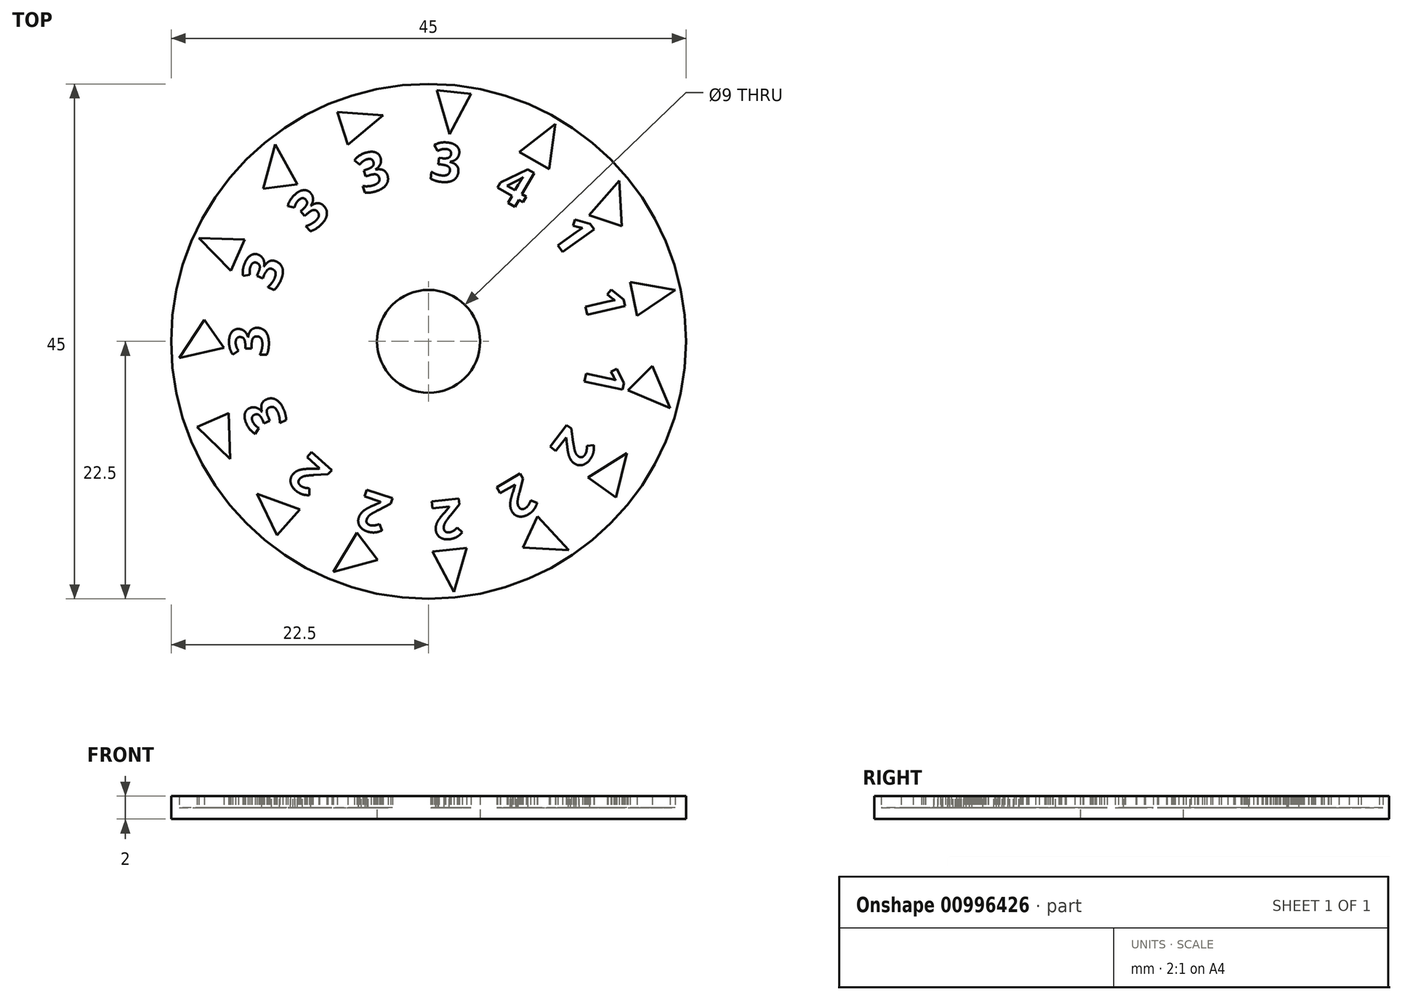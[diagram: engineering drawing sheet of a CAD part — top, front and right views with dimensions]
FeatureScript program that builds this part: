
annotation { "Feature Type Name" : "Feature", "Feature Type Description" : "" }
export const myFeature = defineFeature(function(context is Context, id is Id, definition is map)
    precondition{}
    {
        {
            var Q0;
            Q0=qCreatedBy(makeId("Top.planeOp"),FACE);
            var sketch = newSketch(context, id + "F0", { "sketchPlane" : qUnion([Q0])});
            skCircle(sketch, "E0", {"center": v(0, 0) * mm, "radius": 22.5 * mm});
            skLineSegment(sketch, "E1", {"start": v(0, 0) * mm, "end": v(-20.55, 9.15) * mm, "construction": true});
            skLineSegment(sketch, "E2.1.0", {"start": v(0, 0) * mm, "end": v(-22.5, 0) * mm, "construction": true});
            skLineSegment(sketch, "E2.2.0", {"start": v(0, 0) * mm, "end": v(-20.55, -9.15) * mm, "construction": true});
            skLineSegment(sketch, "E2.3.0", {"start": v(0, 0) * mm, "end": v(-15.06, -16.72) * mm, "construction": true});
            skLineSegment(sketch, "E2.4.0", {"start": v(0, 0) * mm, "end": v(-6.95, -21.4) * mm, "construction": true});
            skLineSegment(sketch, "E2.5.0", {"start": v(0, 0) * mm, "end": v(2.35, -22.38) * mm, "construction": true});
            skLineSegment(sketch, "E2.6.0", {"start": v(0, 0) * mm, "end": v(11.25, -19.49) * mm, "construction": true});
            skLineSegment(sketch, "E2.7.0", {"start": v(0, 0) * mm, "end": v(18.2, -13.23) * mm, "construction": true});
            skLineSegment(sketch, "E2.8.0", {"start": v(0, 0) * mm, "end": v(22, -4.68) * mm, "construction": true});
            skLineSegment(sketch, "E2.9.0", {"start": v(0, 0) * mm, "end": v(22, 4.68) * mm, "construction": true});
            skLineSegment(sketch, "E2.10.0", {"start": v(0, 0) * mm, "end": v(18.2, 13.23) * mm, "construction": true});
            skLineSegment(sketch, "E2.11.0", {"start": v(0, 0) * mm, "end": v(11.25, 19.49) * mm, "construction": true});
            skLineSegment(sketch, "E2.12.0", {"start": v(0, 0) * mm, "end": v(2.35, 22.38) * mm, "construction": true});
            skLineSegment(sketch, "E2.13.0", {"start": v(0, 0) * mm, "end": v(-6.95, 21.4) * mm, "construction": true});
            skLineSegment(sketch, "E2.14.0", {"start": v(0, 0) * mm, "end": v(-15.06, 16.72) * mm, "construction": true});
            skSolve(sketch);
        }
        {
            var Q0;
            Q0=qCreatedBy(makeId("Top.planeOp"),FACE);
            var sketch = newSketch(context, id + "F1", { "sketchPlane" : qUnion([Q0])});
            skCircle(sketch, "E3", {"center": v(0, 0) * mm, "radius": 22.5 * mm});
            skText(sketch, "E4", { "text": "3", "fontName": "OpenSans-Bold.ttf"});
            skLineSegment(sketch, "E5", {"start": v(11.08, 19.01) * mm, "end": v(7.93, 16.55) * mm});
            skLineSegment(sketch, "E6", {"start": v(7.93, 16.55) * mm, "end": v(10.53, 15.05) * mm});
            skLineSegment(sketch, "E7", {"start": v(10.53, 15.05) * mm, "end": v(11.08, 19.01) * mm});
            skPoint(sketch, "E8", {"position": v(9.23, 15.8) * mm});
            skText(sketch, "E9", { "text": "4", "fontName": "OpenSans-Bold.ttf"});
            skCircle(sketch, "E10", {"center": v(0, 0) * mm, "radius": 17.5 * mm, "construction": true});
            skText(sketch, "E11", { "text": "3\n", "fontName": "OpenSans-Bold.ttf"});
            skText(sketch, "E12", { "text": "3", "fontName": "OpenSans-Bold.ttf"});
            skText(sketch, "E13", { "text": "3", "fontName": "OpenSans-Bold.ttf"});
            skText(sketch, "E14", { "text": "3", "fontName": "OpenSans-Bold.ttf"});
            skText(sketch, "E15", { "text": "3", "fontName": "OpenSans-Bold.ttf"});
            skText(sketch, "E16", { "text": "2\n", "fontName": "OpenSans-Bold.ttf"});
            skLineSegment(sketch, "E17.1.0", {"start": v(3.72, 21.63) * mm, "end": v(0.74, 21.94) * mm});
            skLineSegment(sketch, "E17.1.1", {"start": v(1.84, 18.1) * mm, "end": v(3.72, 21.63) * mm});
            skLineSegment(sketch, "E17.1.2", {"start": v(0.74, 21.94) * mm, "end": v(1.84, 18.1) * mm});
            skLineSegment(sketch, "E17.2.0", {"start": v(-7.97, 20.06) * mm, "end": v(-7.04, 17.2) * mm});
            skLineSegment(sketch, "E17.2.1", {"start": v(-3.98, 19.78) * mm, "end": v(-7.97, 20.06) * mm});
            skLineSegment(sketch, "E17.2.2", {"start": v(-7.04, 17.2) * mm, "end": v(-3.98, 19.78) * mm});
            skLineSegment(sketch, "E17.3.0", {"start": v(-14.44, 13.36) * mm, "end": v(-11.47, 13.73) * mm});
            skLineSegment(sketch, "E17.3.1", {"start": v(-13.4, 17.23) * mm, "end": v(-14.44, 13.36) * mm});
            skLineSegment(sketch, "E17.3.2", {"start": v(-11.47, 13.73) * mm, "end": v(-13.4, 17.23) * mm});
            skLineSegment(sketch, "E17.4.0", {"start": v(-17.29, 6.16) * mm, "end": v(-16.07, 8.9) * mm});
            skLineSegment(sketch, "E17.4.1", {"start": v(-20.07, 9.04) * mm, "end": v(-17.29, 6.16) * mm});
            skLineSegment(sketch, "E17.4.2", {"start": v(-16.07, 8.9) * mm, "end": v(-20.07, 9.04) * mm});
            skLineSegment(sketch, "E17.5.0", {"start": v(-17.88, -0.56) * mm, "end": v(-19.6, 1.9) * mm});
            skLineSegment(sketch, "E17.5.1", {"start": v(-21.78, -1.45) * mm, "end": v(-17.88, -0.56) * mm});
            skLineSegment(sketch, "E17.5.2", {"start": v(-19.6, 1.9) * mm, "end": v(-21.78, -1.45) * mm});
            skLineSegment(sketch, "E17.6.0", {"start": v(-17.48, -6.27) * mm, "end": v(-20.22, -7.49) * mm});
            skLineSegment(sketch, "E17.6.1", {"start": v(-17.34, -10.26) * mm, "end": v(-17.48, -6.27) * mm});
            skLineSegment(sketch, "E17.6.2", {"start": v(-20.22, -7.49) * mm, "end": v(-17.34, -10.26) * mm});
            skLineSegment(sketch, "E17.7.0", {"start": v(-13.25, -16.93) * mm, "end": v(-11.24, -14.7) * mm});
            skLineSegment(sketch, "E17.7.1", {"start": v(-15, -13.33) * mm, "end": v(-13.25, -16.93) * mm});
            skLineSegment(sketch, "E17.7.2", {"start": v(-11.24, -14.7) * mm, "end": v(-15, -13.33) * mm});
            skLineSegment(sketch, "E17.8.0", {"start": v(-4.45, -19.11) * mm, "end": v(-6.26, -16.72) * mm});
            skLineSegment(sketch, "E17.8.1", {"start": v(-8.32, -20.15) * mm, "end": v(-4.45, -19.11) * mm});
            skLineSegment(sketch, "E17.8.2", {"start": v(-6.26, -16.72) * mm, "end": v(-8.32, -20.15) * mm});
            skLineSegment(sketch, "E17.9.0", {"start": v(3.31, -18.05) * mm, "end": v(0.33, -18.36) * mm});
            skLineSegment(sketch, "E17.9.1", {"start": v(2.2, -21.9) * mm, "end": v(3.31, -18.05) * mm});
            skLineSegment(sketch, "E17.9.2", {"start": v(0.33, -18.36) * mm, "end": v(2.2, -21.9) * mm});
            skLineSegment(sketch, "E17.10.0", {"start": v(9.51, -15.3) * mm, "end": v(8.24, -18.02) * mm});
            skLineSegment(sketch, "E17.10.1", {"start": v(12.24, -18.23) * mm, "end": v(9.51, -15.3) * mm});
            skLineSegment(sketch, "E17.10.2", {"start": v(8.24, -18.02) * mm, "end": v(12.24, -18.23) * mm});
            skLineSegment(sketch, "E17.11.0", {"start": v(13.94, -11.88) * mm, "end": v(16.37, -13.65) * mm});
            skLineSegment(sketch, "E17.11.1", {"start": v(17.33, -9.76) * mm, "end": v(13.94, -11.88) * mm});
            skLineSegment(sketch, "E17.11.2", {"start": v(16.37, -13.65) * mm, "end": v(17.33, -9.76) * mm});
            skLineSegment(sketch, "E17.13.0", {"start": v(17.6, 5.18) * mm, "end": v(18.23, 2.25) * mm});
            skLineSegment(sketch, "E17.13.1", {"start": v(21.55, 4.48) * mm, "end": v(17.6, 5.18) * mm});
            skLineSegment(sketch, "E17.13.2", {"start": v(18.23, 2.25) * mm, "end": v(21.55, 4.48) * mm});
            skLineSegment(sketch, "E17.14.0", {"start": v(14.03, 11.04) * mm, "end": v(16.87, 10.06) * mm});
            skLineSegment(sketch, "E17.14.1", {"start": v(16.66, 14.06) * mm, "end": v(14.03, 11.04) * mm});
            skLineSegment(sketch, "E17.14.2", {"start": v(16.87, 10.06) * mm, "end": v(16.66, 14.06) * mm});
            skText(sketch, "E18", { "text": "2", "fontName": "OpenSans-Bold.ttf"});
            skText(sketch, "E19", { "text": "2", "fontName": "OpenSans-Bold.ttf"});
            skText(sketch, "E20", { "text": "2", "fontName": "OpenSans-Bold.ttf"});
            skText(sketch, "E21", { "text": "2", "fontName": "OpenSans-Bold.ttf"});
            skText(sketch, "E22", { "text": "1", "fontName": "OpenSans-Bold.ttf"});
            skText(sketch, "E23", { "text": "1", "fontName": "OpenSans-Bold.ttf"});
            skText(sketch, "E24", { "text": "1", "fontName": "OpenSans-Bold.ttf"});
            skCircle(sketch, "E25", {"center": v(0, 0) * mm, "radius": 4.5 * mm});
            skLineSegment(sketch, "E26", {"start": v(21.12, -5.83) * mm, "end": v(19.56, -2.14) * mm});
            skLineSegment(sketch, "E27", {"start": v(19.56, -2.14) * mm, "end": v(17.44, -4.26) * mm});
            skLineSegment(sketch, "E28", {"start": v(17.44, -4.26) * mm, "end": v(21.12, -5.83) * mm});
            const initialGuessF1  = {"E4": [-1e-05, 0.0141, 0.99452, -0.10453, 0.00342], "E9": [0.00561, 0.01288, 0.86603, -0.5, 0.00342], "E11": [-0.0057, 0.01281, 0.95106, 0.30902, 0.00342], "E12": [-0.01036, 0.0094, 0.74314, 0.66913, 0.00342], "E13": [-0.01344, 0.00428, 0.40674, 0.91355, 0.00342], "E14": [-0.014, -0.00134, 0, 1, 0.00342], "E15": [-0.01225, -0.00698, -0.40674, 0.91355, 0.00342], "E16": [-0.00832, -0.01137, -0.74314, 0.66913, 0.00342], "E18": [-0.00298, -0.01377, -0.95106, 0.30902, 0.00342], "E19": [0.00282, -0.01373, -0.99452, -0.10453, 0.00342], "E20": [0.00817, -0.01146, -0.86603, -0.5, 0.00342], "E21": [0.01218, -0.00716, -0.60182, -0.79864, 0.00342], "E22": [0.01403, -0.0016, -0.20791, -0.97815, 0.00342], "E23": [0.01343, 0.00424, 0.22495, -0.97437, 0.00342], "E24": [0.01057, 0.00942, 0.57772, -0.81624, 0.00342]};
            skSetInitialGuess(sketch, initialGuessF1);
            skSolve(sketch);
        }
        {
            var Q0;
            Q0=makeQuery(id+"F1.imprint","IMPRINT",FACE,{"disambiguationData":[TD([[makeQuery(id+"F1.imprint","IMPRINT",EDGE,{"derivedFrom":sQuery(id+"F1.wireOp",EDGE,"E3")}),1.0]])]});
            var Q1;
            Q1=makeQuery(id+"F1.imprint","IMPRINT",FACE,{"disambiguationData":[TD([[makeQuery(id+"F1.imprint","IMPRINT",EDGE,{"derivedFrom":sQuery(id+"F1.wireOp",EDGE,"E9.sketch_text.stroke-11")}),1.0]])]});
            extrude(context, id + "F2", {"entities" : qUnion([Q0, Q1]), "depth" : 2 * mm, "offsetDistance" : 25 * mm});
        }
        {
            var Q0;
            Q0=makeQuery(id+"F1.imprint","IMPRINT",FACE,{"disambiguationData":[TD([[makeQuery(id+"F1.imprint","IMPRINT",EDGE,{"derivedFrom":sQuery(id+"F1.wireOp",EDGE,"E26")}),1.0]])]});
            var Q1;
            Q1=makeQuery(id+"F1.imprint","IMPRINT",FACE,{"disambiguationData":[TD([[makeQuery(id+"F1.imprint","IMPRINT",EDGE,{"derivedFrom":sQuery(id+"F1.wireOp",EDGE,"E17.13.0")}),1.0]])]});
            var Q2;
            Q2=makeQuery(id+"F1.imprint","IMPRINT",FACE,{"disambiguationData":[TD([[makeQuery(id+"F1.imprint","IMPRINT",EDGE,{"derivedFrom":sQuery(id+"F1.wireOp",EDGE,"E17.11.0")}),1.0]])]});
            var Q3;
            Q3=makeQuery(id+"F1.imprint","IMPRINT",FACE,{"disambiguationData":[TD([[makeQuery(id+"F1.imprint","IMPRINT",EDGE,{"derivedFrom":sQuery(id+"F1.wireOp",EDGE,"E21.sketch_text.stroke-0")}),-1.0]])]});
            var Q4;
            Q4=makeQuery(id+"F1.imprint","IMPRINT",FACE,{"disambiguationData":[TD([[makeQuery(id+"F1.imprint","IMPRINT",EDGE,{"derivedFrom":sQuery(id+"F1.wireOp",EDGE,"E20.sketch_text.stroke-0")}),-1.0]])]});
            var Q5;
            Q5=makeQuery(id+"F1.imprint","IMPRINT",FACE,{"disambiguationData":[TD([[makeQuery(id+"F1.imprint","IMPRINT",EDGE,{"derivedFrom":sQuery(id+"F1.wireOp",EDGE,"E19.sketch_text.stroke-0")}),-1.0]])]});
            var Q6;
            Q6=makeQuery(id+"F1.imprint","IMPRINT",FACE,{"disambiguationData":[TD([[makeQuery(id+"F1.imprint","IMPRINT",EDGE,{"derivedFrom":sQuery(id+"F1.wireOp",EDGE,"E18.sketch_text.stroke-0")}),-1.0]])]});
            var Q7;
            Q7=makeQuery(id+"F1.imprint","IMPRINT",FACE,{"disambiguationData":[TD([[makeQuery(id+"F1.imprint","IMPRINT",EDGE,{"derivedFrom":sQuery(id+"F1.wireOp",EDGE,"E17.7.0")}),1.0]])]});
            var Q8;
            Q8=makeQuery(id+"F1.imprint","IMPRINT",FACE,{"disambiguationData":[TD([[makeQuery(id+"F1.imprint","IMPRINT",EDGE,{"derivedFrom":sQuery(id+"F1.wireOp",EDGE,"E17.6.0")}),1.0]])]});
            var Q9;
            Q9=makeQuery(id+"F1.imprint","IMPRINT",FACE,{"disambiguationData":[TD([[makeQuery(id+"F1.imprint","IMPRINT",EDGE,{"derivedFrom":sQuery(id+"F1.wireOp",EDGE,"E17.8.0")}),1.0]])]});
            var Q10;
            Q10=makeQuery(id+"F1.imprint","IMPRINT",FACE,{"disambiguationData":[TD([[makeQuery(id+"F1.imprint","IMPRINT",EDGE,{"derivedFrom":sQuery(id+"F1.wireOp",EDGE,"E17.9.0")}),1.0]])]});
            var Q11;
            Q11=makeQuery(id+"F1.imprint","IMPRINT",FACE,{"disambiguationData":[TD([[makeQuery(id+"F1.imprint","IMPRINT",EDGE,{"derivedFrom":sQuery(id+"F1.wireOp",EDGE,"E17.10.0")}),1.0]])]});
            var Q12;
            Q12=makeQuery(id+"F1.imprint","IMPRINT",FACE,{"disambiguationData":[TD([[makeQuery(id+"F1.imprint","IMPRINT",EDGE,{"derivedFrom":sQuery(id+"F1.wireOp",EDGE,"E17.14.0")}),1.0]])]});
            var Q13;
            Q13=makeQuery(id+"F1.imprint","IMPRINT",FACE,{"disambiguationData":[TD([[makeQuery(id+"F1.imprint","IMPRINT",EDGE,{"derivedFrom":sQuery(id+"F1.wireOp",EDGE,"E5")}),1.0]])]});
            var Q14;
            Q14=makeQuery(id+"F1.imprint","IMPRINT",FACE,{"disambiguationData":[TD([[makeQuery(id+"F1.imprint","IMPRINT",EDGE,{"derivedFrom":sQuery(id+"F1.wireOp",EDGE,"E17.5.0")}),1.0]])]});
            var Q15;
            Q15=makeQuery(id+"F1.imprint","IMPRINT",FACE,{"disambiguationData":[TD([[makeQuery(id+"F1.imprint","IMPRINT",EDGE,{"derivedFrom":sQuery(id+"F1.wireOp",EDGE,"E17.4.0")}),1.0]])]});
            var Q16;
            Q16=makeQuery(id+"F1.imprint","IMPRINT",FACE,{"disambiguationData":[TD([[makeQuery(id+"F1.imprint","IMPRINT",EDGE,{"derivedFrom":sQuery(id+"F1.wireOp",EDGE,"E17.3.0")}),1.0]])]});
            var Q17;
            Q17=makeQuery(id+"F1.imprint","IMPRINT",FACE,{"disambiguationData":[TD([[makeQuery(id+"F1.imprint","IMPRINT",EDGE,{"derivedFrom":sQuery(id+"F1.wireOp",EDGE,"E17.2.0")}),1.0]])]});
            var Q18;
            Q18=makeQuery(id+"F1.imprint","IMPRINT",FACE,{"disambiguationData":[TD([[makeQuery(id+"F1.imprint","IMPRINT",EDGE,{"derivedFrom":sQuery(id+"F1.wireOp",EDGE,"E17.1.0")}),1.0]])]});
            var Q19;
            Q19=makeQuery(id+"F1.imprint","IMPRINT",FACE,{"disambiguationData":[TD([[makeQuery(id+"F1.imprint","IMPRINT",EDGE,{"derivedFrom":sQuery(id+"F1.wireOp",EDGE,"E11.sketch_text.stroke-0")}),-1.0]])]});
            var Q20;
            Q20=makeQuery(id+"F1.imprint","IMPRINT",FACE,{"disambiguationData":[TD([[makeQuery(id+"F1.imprint","IMPRINT",EDGE,{"derivedFrom":sQuery(id+"F1.wireOp",EDGE,"E4.sketch_text.stroke-0")}),-1.0]])]});
            var Q21;
            Q21=makeQuery(id+"F1.imprint","IMPRINT",FACE,{"disambiguationData":[TD([[makeQuery(id+"F1.imprint","IMPRINT",EDGE,{"derivedFrom":sQuery(id+"F1.wireOp",EDGE,"E9.sketch_text.stroke-0")}),-1.0]])]});
            var Q22;
            Q22=makeQuery(id+"F1.imprint","IMPRINT",FACE,{"disambiguationData":[TD([[makeQuery(id+"F1.imprint","IMPRINT",EDGE,{"derivedFrom":sQuery(id+"F1.wireOp",EDGE,"E12.sketch_text.stroke-0")}),-1.0]])]});
            var Q23;
            Q23=makeQuery(id+"F1.imprint","IMPRINT",FACE,{"disambiguationData":[TD([[makeQuery(id+"F1.imprint","IMPRINT",EDGE,{"derivedFrom":sQuery(id+"F1.wireOp",EDGE,"E13.sketch_text.stroke-0")}),-1.0]])]});
            var Q24;
            Q24=makeQuery(id+"F1.imprint","IMPRINT",FACE,{"disambiguationData":[TD([[makeQuery(id+"F1.imprint","IMPRINT",EDGE,{"derivedFrom":sQuery(id+"F1.wireOp",EDGE,"E14.sketch_text.stroke-0")}),-1.0]])]});
            var Q25;
            Q25=makeQuery(id+"F1.imprint","IMPRINT",FACE,{"disambiguationData":[TD([[makeQuery(id+"F1.imprint","IMPRINT",EDGE,{"derivedFrom":sQuery(id+"F1.wireOp",EDGE,"E15.sketch_text.stroke-0")}),-1.0]])]});
            var Q26;
            Q26=makeQuery(id+"F1.imprint","IMPRINT",FACE,{"disambiguationData":[TD([[makeQuery(id+"F1.imprint","IMPRINT",EDGE,{"derivedFrom":sQuery(id+"F1.wireOp",EDGE,"E16.sketch_text.stroke-0")}),-1.0]])]});
            var Q27;
            Q27=makeQuery(id+"F1.imprint","IMPRINT",FACE,{"disambiguationData":[TD([[makeQuery(id+"F1.imprint","IMPRINT",EDGE,{"derivedFrom":sQuery(id+"F1.wireOp",EDGE,"E22.sketch_text.stroke-0")}),-1.0]])]});
            var Q28;
            Q28=makeQuery(id+"F1.imprint","IMPRINT",FACE,{"disambiguationData":[TD([[makeQuery(id+"F1.imprint","IMPRINT",EDGE,{"derivedFrom":sQuery(id+"F1.wireOp",EDGE,"E23.sketch_text.stroke-0")}),-1.0]])]});
            var Q29;
            Q29=makeQuery(id+"F1.imprint","IMPRINT",FACE,{"disambiguationData":[TD([[makeQuery(id+"F1.imprint","IMPRINT",EDGE,{"derivedFrom":sQuery(id+"F1.wireOp",EDGE,"E24.sketch_text.stroke-0")}),-1.0]])]});
            extrude(context, id + "F3", {"entities" : qUnion([Q0, Q1, Q2, Q3, Q4, Q5, Q6, Q7, Q8, Q9, Q10, Q11, Q12, Q13, Q14, Q15, Q16, Q17, Q18, Q19, Q20, Q21, Q22, Q23, Q24, Q25, Q26, Q27, Q28, Q29]), "operationType" : NewBodyOperationType.ADD, "depth" : 1 * mm, "offsetDistance" : 25 * mm});
        }
    });
